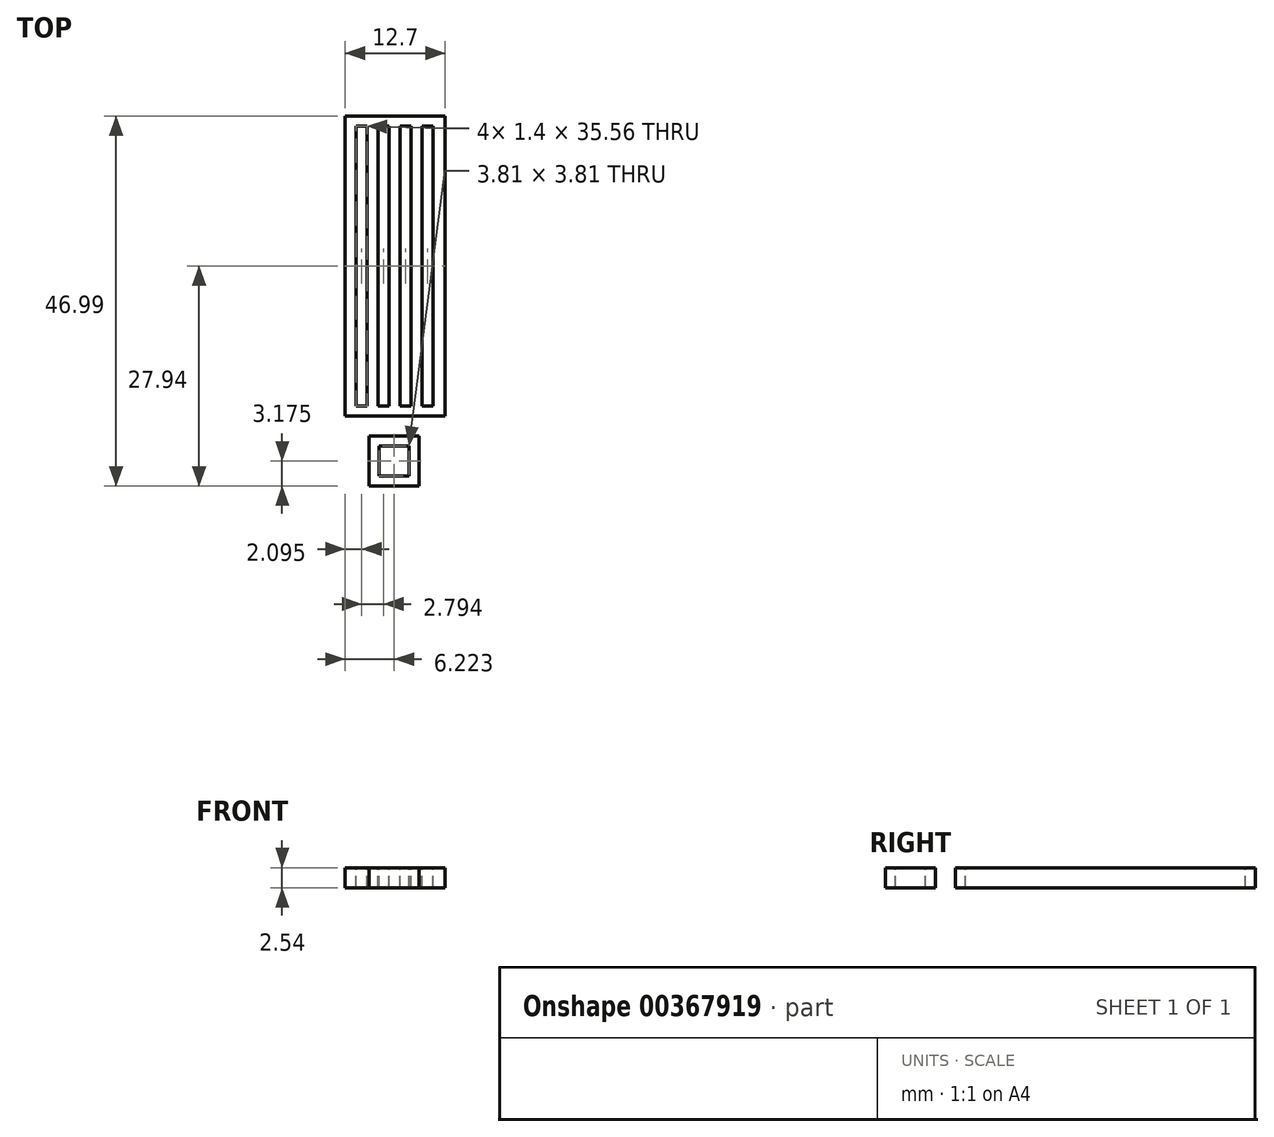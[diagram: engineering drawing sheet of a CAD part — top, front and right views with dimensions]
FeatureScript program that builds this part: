
annotation { "Feature Type Name" : "Feature", "Feature Type Description" : "" }
export const myFeature = defineFeature(function(context is Context, id is Id, definition is map)
    precondition{}
    {
        {
            var Q0;
            Q0=qCreatedBy(makeId("Top.planeOp"),FACE);
            var sketch = newSketch(context, id + "F0", { "sketchPlane" : qUnion([Q0])});
            skLineSegment(sketch, "E0.bottom", {"start": v(-6.35, 25.4) * mm, "end": v(6.35, 25.4) * mm});
            skLineSegment(sketch, "E0.top", {"start": v(-6.35, -12.7) * mm, "end": v(6.35, -12.7) * mm});
            skLineSegment(sketch, "E0.left", {"start": v(-6.35, 25.4) * mm, "end": v(-6.35, -12.7) * mm});
            skLineSegment(sketch, "E0.right", {"start": v(6.35, 25.4) * mm, "end": v(6.35, -12.7) * mm});
            skLineSegment(sketch, "E1.bottom", {"start": v(-1.27, -12.7) * mm, "end": v(1.27, -12.7) * mm});
            skLineSegment(sketch, "E1.top", {"start": v(-1.27, -15.24) * mm, "end": v(1.27, -15.24) * mm});
            skLineSegment(sketch, "E1.left", {"start": v(-1.27, -12.7) * mm, "end": v(-1.27, -15.24) * mm});
            skLineSegment(sketch, "E1.right", {"start": v(1.27, -12.7) * mm, "end": v(1.27, -15.24) * mm});
            skLineSegment(sketch, "E2.bottom", {"start": v(-3.3, -15.24) * mm, "end": v(3.05, -15.24) * mm});
            skLineSegment(sketch, "E2.top", {"start": v(-3.3, -21.6) * mm, "end": v(3.05, -21.6) * mm});
            skLineSegment(sketch, "E2.left", {"start": v(-3.3, -15.24) * mm, "end": v(-3.3, -21.6) * mm});
            skLineSegment(sketch, "E2.right", {"start": v(3.05, -15.24) * mm, "end": v(3.05, -21.6) * mm});
            skSolve(sketch);
        }
        {
            var Q0;
            Q0=makeQuery(id+"F0.imprint","IMPRINT",FACE,{"disambiguationData":[TD([[makeQuery(id+"F0.imprint","IMPRINT",EDGE,{"derivedFrom":sQuery(id+"F0.wireOp",EDGE,"E0.bottom")}),-1.0]])]});
            var Q1;
            Q1=makeQuery(id+"F0.imprint","IMPRINT",FACE,{"disambiguationData":[TD([[makeQuery(id+"F0.imprint","IMPRINT",EDGE,{"derivedFrom":sQuery(id+"F0.wireOp",EDGE,"E1.bottom")}),-1.0]])]});
            var Q2;
            Q2=makeQuery(id+"F0.imprint","IMPRINT",FACE,{"disambiguationData":[TD([[makeQuery(id+"F0.imprint","IMPRINT",EDGE,{"derivedFrom":sQuery(id+"F0.wireOp",EDGE,"E2.top")}),1.0]])]});
            extrude(context, id + "F1", {"entities" : qUnion([Q0, Q1, Q2]), "depth" : 2.54 * mm});
        }
        {
            var Q0;
            Q0=makeQuery(id+"F1.opExtrude","CAP_FACE",FACE,{"disambiguationData":[OSD([sQuery(id+"F0.wireOp",EDGE,"E0.bottom"),sQuery(id+"F0.wireOp",EDGE,"E0.top"),sQuery(id+"F0.wireOp",EDGE,"E0.left"),sQuery(id+"F0.wireOp",EDGE,"E0.right"),sQuery(id+"F0.wireOp",EDGE,"E1.left"),sQuery(id+"F0.wireOp",EDGE,"E1.right"),sQuery(id+"F0.wireOp",EDGE,"E2.bottom"),sQuery(id+"F0.wireOp",EDGE,"E2.top"),sQuery(id+"F0.wireOp",EDGE,"E2.left"),sQuery(id+"F0.wireOp",EDGE,"E2.right")])],"isStart":false});
            var sketch = newSketch(context, id + "F2", { "sketchPlane" : qUnion([Q0])});
            skLineSegment(sketch, "E3.bottom", {"start": v(-4.95, 24.13) * mm, "end": v(-3.56, 24.13) * mm});
            skLineSegment(sketch, "E3.top", {"start": v(-4.95, -11.43) * mm, "end": v(-3.56, -11.43) * mm});
            skLineSegment(sketch, "E3.left", {"start": v(-4.95, 24.13) * mm, "end": v(-4.95, -11.43) * mm});
            skLineSegment(sketch, "E3.right", {"start": v(-3.56, 24.13) * mm, "end": v(-3.56, -11.43) * mm});
            skLineSegment(sketch, "E4.bottom", {"start": v(-2.16, 24.13) * mm, "end": v(-0.76, 24.13) * mm});
            skLineSegment(sketch, "E4.top", {"start": v(-2.16, -11.43) * mm, "end": v(-0.76, -11.43) * mm});
            skLineSegment(sketch, "E4.left", {"start": v(-2.16, 24.13) * mm, "end": v(-2.16, -11.43) * mm});
            skLineSegment(sketch, "E4.right", {"start": v(-0.76, 24.13) * mm, "end": v(-0.76, -11.43) * mm});
            skPoint(sketch, "E5.oppositeSnap0", {"position": v(3.81, -12.7) * mm});
            skLineSegment(sketch, "E6.bottom", {"start": v(0.64, 24.13) * mm, "end": v(2.03, 24.13) * mm});
            skLineSegment(sketch, "E6.top", {"start": v(0.64, -11.43) * mm, "end": v(2.03, -11.43) * mm});
            skLineSegment(sketch, "E6.left", {"start": v(0.64, 24.13) * mm, "end": v(0.64, -11.43) * mm});
            skLineSegment(sketch, "E6.right", {"start": v(2.03, 24.13) * mm, "end": v(2.03, -11.43) * mm});
            skLineSegment(sketch, "E7.bottom", {"start": v(4.83, 24.13) * mm, "end": v(3.43, 24.13) * mm});
            skLineSegment(sketch, "E7.top", {"start": v(4.83, -11.43) * mm, "end": v(3.43, -11.43) * mm});
            skLineSegment(sketch, "E7.left", {"start": v(4.83, 24.13) * mm, "end": v(4.83, -11.43) * mm});
            skLineSegment(sketch, "E7.right", {"start": v(3.43, 24.13) * mm, "end": v(3.43, -11.43) * mm});
            skSolve(sketch);
        }
        {
            var Q0;
            Q0=makeQuery(id+"F2.imprint","IMPRINT",FACE,{"disambiguationData":[TD([[makeQuery(id+"F2.imprint","IMPRINT",EDGE,{"derivedFrom":sQuery(id+"F2.wireOp",EDGE,"E3.bottom")}),-1.0]])]});
            var Q1;
            Q1=makeQuery(id+"F2.imprint","IMPRINT",FACE,{"disambiguationData":[TD([[makeQuery(id+"F2.imprint","IMPRINT",EDGE,{"derivedFrom":sQuery(id+"F2.wireOp",EDGE,"E4.bottom")}),-1.0]])]});
            var Q2;
            Q2=makeQuery(id+"F2.imprint","IMPRINT",FACE,{"disambiguationData":[TD([[makeQuery(id+"F2.imprint","IMPRINT",EDGE,{"derivedFrom":sQuery(id+"F2.wireOp",EDGE,"E6.bottom")}),-1.0]])]});
            var Q3;
            Q3=makeQuery(id+"F2.imprint","IMPRINT",FACE,{"disambiguationData":[TD([[makeQuery(id+"F2.imprint","IMPRINT",EDGE,{"derivedFrom":sQuery(id+"F2.wireOp",EDGE,"E7.bottom")}),1.0]])]});
            extrude(context, id + "F3", {"entities" : qUnion([Q0, Q1, Q2, Q3]), "operationType" : NewBodyOperationType.REMOVE, "endBound" : BoundingType.THROUGH_ALL, "oppositeDirection" : true, "depth" : 25.4 * mm});
        }
        {
            var Q0;
            Q0=makeQuery(id+"F1.opExtrude","CAP_FACE",FACE,{"disambiguationData":[OSD([sQuery(id+"F0.wireOp",EDGE,"E0.bottom"),sQuery(id+"F0.wireOp",EDGE,"E0.top"),sQuery(id+"F0.wireOp",EDGE,"E0.left"),sQuery(id+"F0.wireOp",EDGE,"E0.right"),sQuery(id+"F0.wireOp",EDGE,"E1.left"),sQuery(id+"F0.wireOp",EDGE,"E1.right"),sQuery(id+"F0.wireOp",EDGE,"E2.bottom"),sQuery(id+"F0.wireOp",EDGE,"E2.top"),sQuery(id+"F0.wireOp",EDGE,"E2.left"),sQuery(id+"F0.wireOp",EDGE,"E2.right")])],"isStart":false});
            var sketch = newSketch(context, id + "F4", { "sketchPlane" : qUnion([Q0])});
            skLineSegment(sketch, "E8.bottom", {"start": v(-2.03, -16.51) * mm, "end": v(1.78, -16.51) * mm});
            skLineSegment(sketch, "E8.top", {"start": v(-2.03, -20.32) * mm, "end": v(1.78, -20.32) * mm});
            skLineSegment(sketch, "E8.left", {"start": v(-2.03, -16.51) * mm, "end": v(-2.03, -20.32) * mm});
            skLineSegment(sketch, "E8.right", {"start": v(1.78, -16.51) * mm, "end": v(1.78, -20.32) * mm});
            skSolve(sketch);
        }
        {
            var Q0;
            Q0=makeQuery(id+"F4.imprint","IMPRINT",FACE,{"disambiguationData":[TD([[makeQuery(id+"F4.imprint","IMPRINT",EDGE,{"derivedFrom":sQuery(id+"F4.wireOp",EDGE,"E8.bottom")}),-1.0]])]});
            extrude(context, id + "F5", {"entities" : qUnion([Q0]), "operationType" : NewBodyOperationType.REMOVE, "endBound" : BoundingType.THROUGH_ALL, "oppositeDirection" : true, "depth" : 25.4 * mm});
        }
    });
